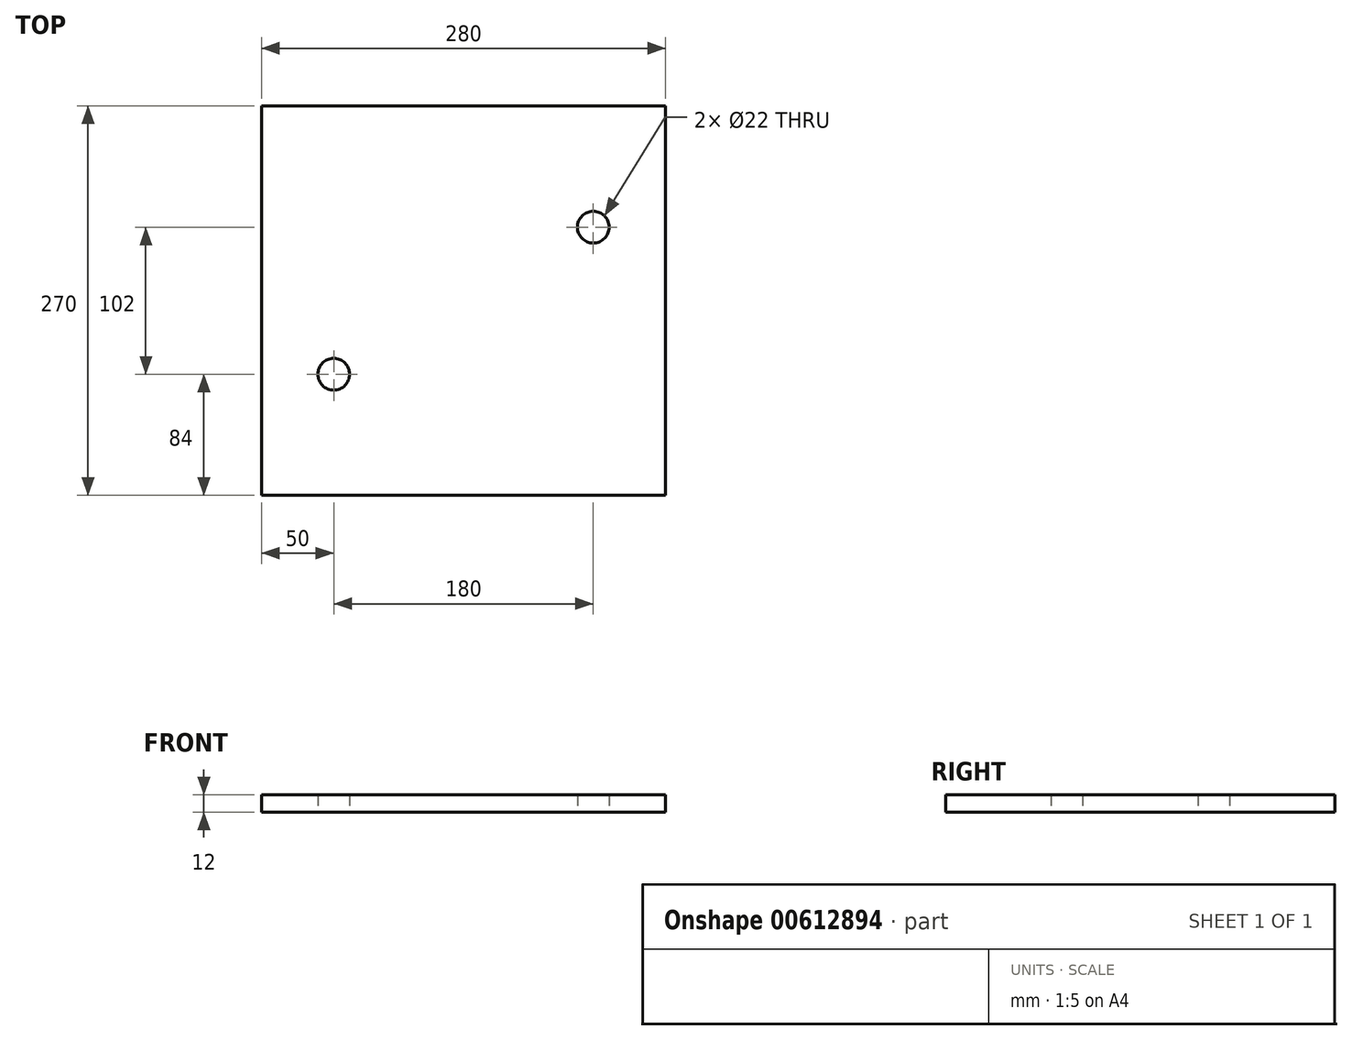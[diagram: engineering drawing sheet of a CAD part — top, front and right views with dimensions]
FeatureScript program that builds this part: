
annotation { "Feature Type Name" : "Feature", "Feature Type Description" : "" }
export const myFeature = defineFeature(function(context is Context, id is Id, definition is map)
    precondition{}
    {
        {
            var Q0;
            Q0=qCreatedBy(makeId("Top.planeOp"),FACE);
            var sketch = newSketch(context, id + "F0", { "sketchPlane" : qUnion([Q0])});
            skLineSegment(sketch, "E0.bottom", {"start": v(140, 135) * mm, "end": v(-140, 135) * mm});
            skLineSegment(sketch, "E0.top", {"start": v(140, -135) * mm, "end": v(-140, -135) * mm});
            skLineSegment(sketch, "E0.left", {"start": v(140, 135) * mm, "end": v(140, -135) * mm});
            skLineSegment(sketch, "E0.right", {"start": v(-140, 135) * mm, "end": v(-140, -135) * mm});
            skPoint(sketch, "E0.middle", {"position": v(0, 0) * mm});
            skCircle(sketch, "E1", {"center": v(90, 51) * mm, "radius": 11 * mm});
            skCircle(sketch, "E2", {"center": v(-90, -51) * mm, "radius": 11 * mm});
            skSolve(sketch);
        }
        {
            var Q0;
            Q0=makeQuery(id+"F0.imprint","IMPRINT",FACE,{"disambiguationData":[TD([[makeQuery(id+"F0.imprint","IMPRINT",EDGE,{"derivedFrom":sQuery(id+"F0.wireOp",EDGE,"E0.bottom")}),1.0]])]});
            extrude(context, id + "F1", {"entities" : qUnion([Q0]), "endBound" : BoundingType.SYMMETRIC, "depth" : 12 * mm, "offsetDistance" : 25 * mm});
        }
    });
